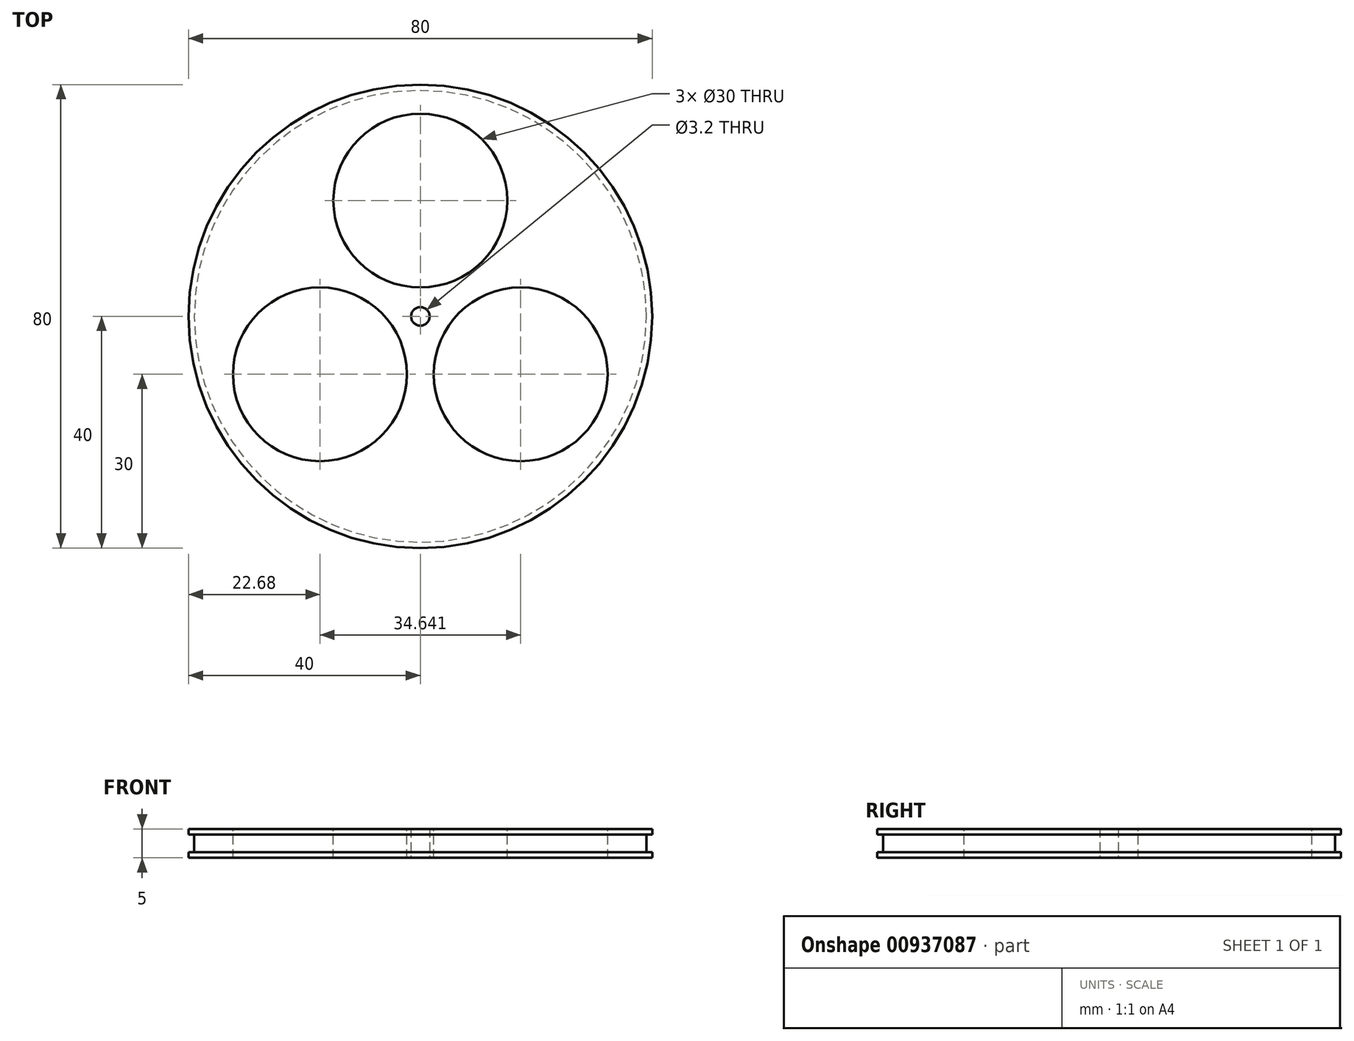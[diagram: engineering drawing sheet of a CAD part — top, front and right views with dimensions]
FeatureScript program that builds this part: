
annotation { "Feature Type Name" : "Feature", "Feature Type Description" : "" }
export const myFeature = defineFeature(function(context is Context, id is Id, definition is map)
    precondition{}
    {
        {
            var Q0;
            Q0=qCreatedBy(makeId("Top.planeOp"),FACE);
            var sketch = newSketch(context, id + "F0", { "sketchPlane" : qUnion([Q0])});
            skCircle(sketch, "E0", {"center": v(0, 0) * mm, "radius": 40 * mm});
            skCircle(sketch, "E1", {"center": v(0, 0) * mm, "radius": 1.6 * mm});
            skPoint(sketch, "E2.0.midPoint", {"position": v(30, 0) * mm});
            skSolve(sketch);
        }
        {
            var Q0;
            Q0=qSketchRegion(id+"F0",true);
            extrude(context, id + "F1", {"entities" : qUnion([Q0]), "depth" : 5 * mm, "offsetDistance" : 25 * mm});
        }
        {
            var Q0;
            Q0=qCreatedBy(makeId("Right.planeOp"),FACE);
            var sketch = newSketch(context, id + "F2", { "sketchPlane" : qUnion([Q0])});
            skLineSegment(sketch, "E3.bottom", {"start": v(40, 4) * mm, "end": v(39, 4) * mm});
            skLineSegment(sketch, "E3.top", {"start": v(40, 1) * mm, "end": v(39, 1) * mm});
            skLineSegment(sketch, "E3.left", {"start": v(40, 4) * mm, "end": v(40, 1) * mm});
            skLineSegment(sketch, "E3.right", {"start": v(39, 4) * mm, "end": v(39, 1) * mm});
            skLineSegment(sketch, "E4", {"start": v(40, 5) * mm, "end": v(40, 0) * mm, "construction": true});
            skLineSegment(sketch, "E5", {"start": v(-40, 0) * mm, "end": v(-40, 5) * mm});
            skSolve(sketch);
        }
        {
            var Q0;
            Q0=qSketchRegion(id+"F2",true);
            var Q1;
            Q1=makeQuery(id+"F1.opExtrude","CAP_EDGE",EDGE,{"disambiguationData":[OSD([sQuery(id+"F0.wireOp",EDGE,"E0")])],"isStart":false});
            revolve(context, id + "F3", {"operationType" : NewBodyOperationType.REMOVE, "surfaceOperationType" : NewSurfaceOperationType.NEW, "entities" : qUnion([Q0]), "axis" : qUnion([Q1]), "revolveType" : RevolveType.FULL, "oppositeDirection" : true});
        }
        {
            var Q0;
            Q0=makeQuery(id+"F1.opExtrude","CAP_FACE",FACE,{"disambiguationData":[OSD([sQuery(id+"F0.wireOp",EDGE,"E0"),sQuery(id+"F0.wireOp",EDGE,"E1")])],"isStart":false});
            var sketch = newSketch(context, id + "F4", { "sketchPlane" : qUnion([Q0])});
            skCircle(sketch, "E6", {"center": v(0, 20) * mm, "radius": 15 * mm});
            skCircle(sketch, "E7.1.0", {"center": v(-17.32, -10) * mm, "radius": 15 * mm});
            skCircle(sketch, "E7.2.0", {"center": v(17.32, -10) * mm, "radius": 15 * mm});
            skPoint(sketch, "E7.center", {"position": v(0, 0) * mm});
            skLineSegment(sketch, "E8", {"start": v(-40, 0) * mm, "end": v(40, 0) * mm, "construction": true});
            skSolve(sketch);
        }
        {
            var Q0;
            Q0=qSketchRegion(id+"F4",true);
            extrude(context, id + "F5", {"entities" : qUnion([Q0]), "operationType" : NewBodyOperationType.REMOVE, "oppositeDirection" : true, "depth" : 25 * mm, "offsetDistance" : 25 * mm});
        }
    });
